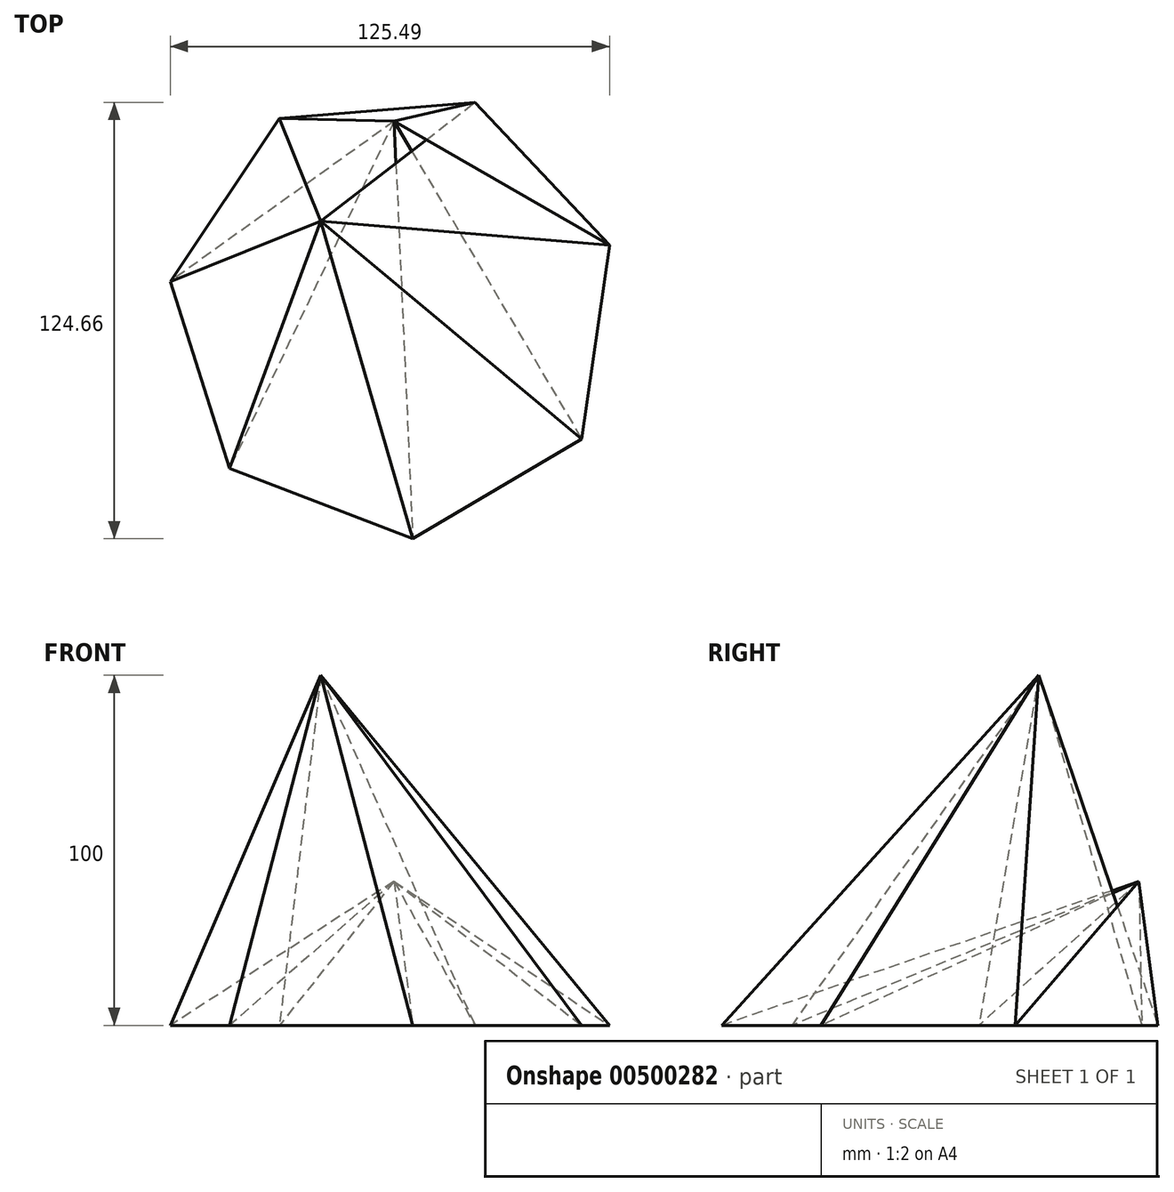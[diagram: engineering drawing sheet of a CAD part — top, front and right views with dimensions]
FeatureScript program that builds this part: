
annotation { "Feature Type Name" : "Feature", "Feature Type Description" : "" }
export const myFeature = defineFeature(function(context is Context, id is Id, definition is map)
    precondition{}
    {
        {
            var Q0;
            Q0=qCreatedBy(makeId("Top.planeOp"),FACE);
            var sketch = newSketch(context, id + "F0", { "sketchPlane" : qUnion([Q0])});
            skCircle(sketch, "E0.cCircle", {"center": v(0, 0) * mm, "radius": 64.58 * mm, "construction": true});
            skLineSegment(sketch, "E0.0", {"start": v(-32.73, 55.67) * mm, "end": v(23.12, 60.3) * mm});
            skLineSegment(sketch, "E0.1", {"start": v(23.12, 60.3) * mm, "end": v(61.56, 19.52) * mm});
            skLineSegment(sketch, "E0.2", {"start": v(61.56, 19.52) * mm, "end": v(53.64, -35.96) * mm});
            skLineSegment(sketch, "E0.3", {"start": v(53.64, -35.96) * mm, "end": v(5.34, -64.36) * mm});
            skLineSegment(sketch, "E0.4", {"start": v(5.34, -64.36) * mm, "end": v(-47, -44.3) * mm});
            skLineSegment(sketch, "E0.5", {"start": v(-47, -44.3) * mm, "end": v(-63.93, 9.12) * mm});
            skLineSegment(sketch, "E0.6", {"start": v(-63.93, 9.12) * mm, "end": v(-32.73, 55.67) * mm});
            skSolve(sketch);
        }
        {
            var Q0;
            Q0=qCreatedBy(makeId("Top.planeOp"),FACE);
            cPlane(context, id + "F1", {"entities" : qUnion([Q0]), "cplaneType" : CPlaneType.OFFSET, "offset" : 100 * mm, "width" : 152.4 * mm, "height" : 152.4 * mm});
        }
        {
            var Q0;
            Q0=qCreatedBy(id+"F1.planeOp",FACE);
            var sketch = newSketch(context, id + "F2", { "sketchPlane" : qUnion([Q0])});
            skPoint(sketch, "E1", {"position": v(-20.9, 26.27) * mm});
            skSolve(sketch);
        }
        {
            var Q0;
            Q0=sQuery(id+"F2.wireOp",VERTEX,"E1");
            var Q1;
            Q1=makeQuery(id+"F0.imprint","IMPRINT",FACE,{"disambiguationData":[TD([[makeQuery(id+"F0.imprint","IMPRINT",EDGE,{"derivedFrom":sQuery(id+"F0.wireOp",EDGE,"E0.0")}),-1.0]])]});
            loft(context, id + "F3", {"sheetProfilesArray" : [{ "sheetProfileEntities" : qUnion([Q0]) }, { "sheetProfileEntities" : qUnion([Q1]) }]});
        }
        {
            var Q0;
            Q0=qCreatedBy(makeId("Right.planeOp"),FACE);
            var sketch = newSketch(context, id + "F4", { "sketchPlane" : qUnion([Q0])});
            skPoint(sketch, "E2", {"position": v(54.86, 41.12) * mm});
            skPoint(sketch, "E3", {"position": v(-33.57, -41.32) * mm});
            skSolve(sketch);
        }
        {
            var Q0;
            Q0=sQuery(id+"F4.wireOp",VERTEX,"E2");
            var Q1;
            Q1=makeQuery(id+"F3.opLoft","CAP_FACE",FACE,{"disambiguationData":[OSD([makeQuery(id+"F0.imprint","IMPRINT",FACE,{"disambiguationData":[TD([[makeQuery(id+"F0.imprint","IMPRINT",EDGE,{"derivedFrom":sQuery(id+"F0.wireOp",EDGE,"E0.0")}),-1.0]])]})])],"isStart":true});
            loft(context, id + "F5", {"sheetProfilesArray" : [{ "sheetProfileEntities" : qUnion([Q0]) }, { "sheetProfileEntities" : qUnion([Q1]) }]});
        }
    });
